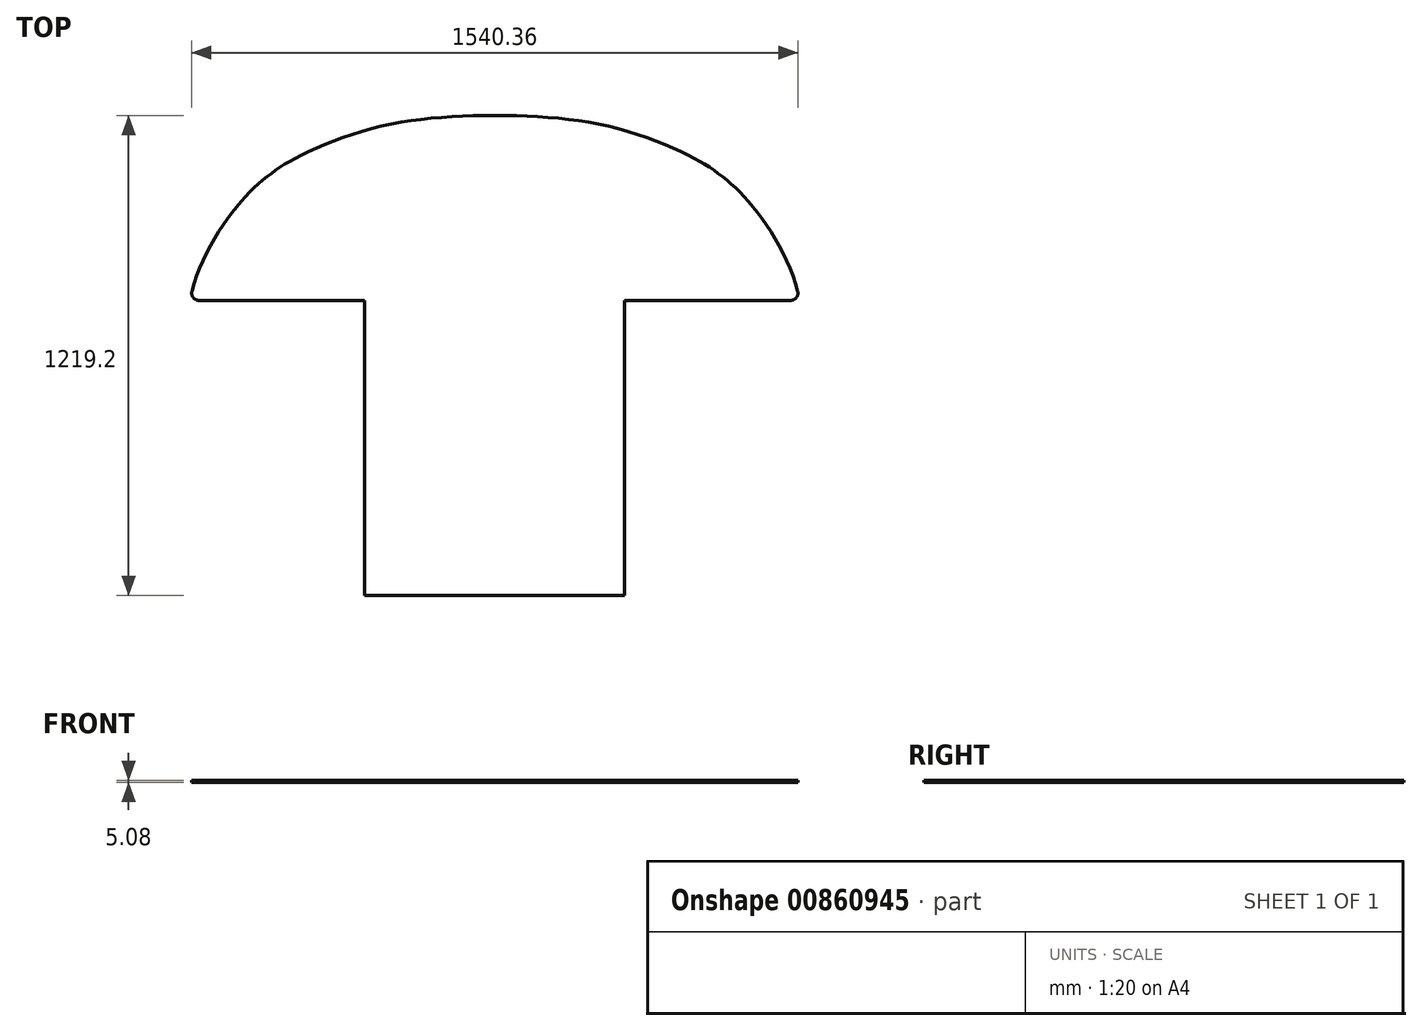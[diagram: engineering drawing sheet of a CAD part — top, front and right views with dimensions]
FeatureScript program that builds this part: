
annotation { "Feature Type Name" : "Feature", "Feature Type Description" : "" }
export const myFeature = defineFeature(function(context is Context, id is Id, definition is map)
    precondition{}
    {
        {
            var Q0;
            Q0=qCreatedBy(makeId("Top.planeOp"),FACE);
            var sketch = newSketch(context, id + "F0", { "sketchPlane" : qUnion([Q0])});
            skLineSegment(sketch, "E0", {"start": v(0, 0) * mm, "end": v(330.2, 0) * mm, "construction": true});
            skLineSegment(sketch, "E1", {"start": v(330.2, 0) * mm, "end": v(330.2, -749.3) * mm});
            skLineSegment(sketch, "E2", {"start": v(330.2, -749.3) * mm, "end": v(0, -749.3) * mm});
            skLineSegment(sketch, "E3", {"start": v(0, -749.3) * mm, "end": v(0, 0) * mm});
            skLineSegment(sketch, "E4", {"start": v(0, 0) * mm, "end": v(0, 469.9) * mm});
            skLineSegment(sketch, "E5", {"start": v(330.2, 0) * mm, "end": v(774.7, 0) * mm});
            skLineSegment(sketch, "E6", {"start": v(774.7, 0) * mm, "end": v(711.05, 360.97) * mm, "construction": true});
            skLineSegment(sketch, "E7", {"start": v(533.4, 0) * mm, "end": v(533.4, 346.08) * mm, "construction": true});
            skLineSegment(sketch, "E8", {"start": v(647.7, 0) * mm, "end": v(647.7, 247.65) * mm, "construction": true});
            skLineSegment(sketch, "E9", {"start": v(330.2, 0) * mm, "end": v(330.2, 431.8) * mm, "construction": true});
            skLineSegment(sketch, "E10", {"start": v(-111.1, 469.9) * mm, "end": v(0, 469.9) * mm, "construction": true});
            skFitSpline(sketch, "E11", {"points": [v(0, 469.9) * mm, v(330.2, 431.8) * mm, v(774.7, 0) * mm], "startDerivative": vector(198.15, 0) * mm, "endDerivative": vector(216.3, -1226.69) * mm, "construction": true});
            skFitSpline(sketch, "E12", {"points": [v(0, 469.9) * mm, v(330.2, 431.8) * mm, v(533.4, 346.08) * mm], "startDerivative": vector(640.52, 0) * mm, "endDerivative": vector(245.35, -152.34) * mm});
            skFitSpline(sketch, "E13", {"points": [v(533.4, 346.08) * mm, v(647.7, 247.65) * mm, v(774.7, 0) * mm], "startDerivative": vector(285.28, -177.13) * mm, "endDerivative": vector(83.47, -473.38) * mm});
            skSolve(sketch);
        }
        {
            var Q0;
            Q0=makeQuery(id+"F0.imprint","IMPRINT",FACE,{"disambiguationData":[TD([[makeQuery(id+"F0.imprint","IMPRINT",EDGE,{"derivedFrom":sQuery(id+"F0.wireOp",EDGE,"E1")}),-1.0]])]});
            extrude(context, id + "F1", {"entities" : qUnion([Q0]), "depth" : 5.08 * mm});
        }
        {
            var Q0;
            Q0=makeQuery(id+"F1.opExtrude","SWEPT_BODY",BODY,{"disambiguationData":[OSD([sQuery(id+"F0.wireOp",EDGE,"E1"),sQuery(id+"F0.wireOp",EDGE,"E2"),sQuery(id+"F0.wireOp",EDGE,"E3"),sQuery(id+"F0.wireOp",EDGE,"E4"),sQuery(id+"F0.wireOp",EDGE,"E5"),sQuery(id+"F0.wireOp",EDGE,"E12"),sQuery(id+"F0.wireOp",EDGE,"E13")])]});
            var Q1;
            Q1=makeQuery(id+"F1.opExtrude","SWEPT_FACE",FACE,{"disambiguationData":[OSD([sQuery(id+"F0.wireOp",EDGE,"E3"),sQuery(id+"F0.wireOp",EDGE,"E4")])]});
            mirror(context, id + "F2", {"operationType" : NewBodyOperationType.ADD, "entities" : qUnion([Q0]), "mirrorPlane" : qUnion([Q1])});
        }
        {
            var Q0;
            Q0=makeQuery(id+"F1.opExtrude","SWEPT_EDGE",EDGE,{"disambiguationData":[OSD([sQuery(id+"F0.wireOp",EDGE,"E5"),sQuery(id+"F0.wireOp",EDGE,"E13")])]});
            var Q1;
            Q1=makeQuery(id+"F2.opPattern","COPY",EDGE,{"derivedFrom":makeQuery(id+"F1.opExtrude","SWEPT_EDGE",EDGE,{"disambiguationData":[OSD([sQuery(id+"F0.wireOp",EDGE,"E5"),sQuery(id+"F0.wireOp",EDGE,"E13")])]}),"instanceName":"1"});
            fillet(context, id + "F3", {"entities" : qUnion([Q0, Q1]), "radius" : 19.05 * mm, "tangentPropagation" : true, "allowEdgeOverflow" : false});
        }
    });
